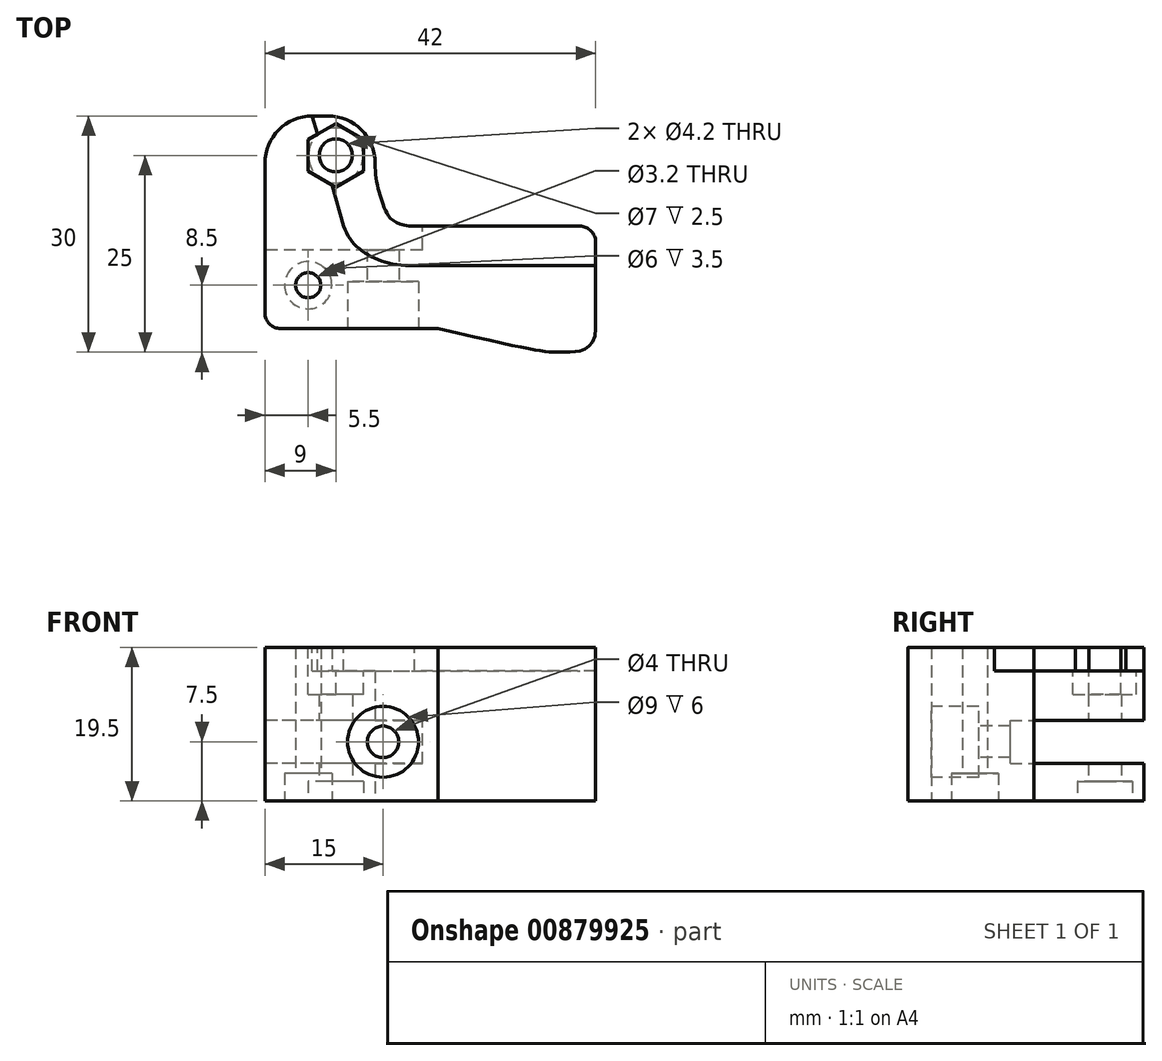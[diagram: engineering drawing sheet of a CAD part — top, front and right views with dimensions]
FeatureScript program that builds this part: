
annotation { "Feature Type Name" : "Feature", "Feature Type Description" : "" }
export const myFeature = defineFeature(function(context is Context, id is Id, definition is map)
    precondition{}
    {
        {
            var Q0;
            Q0=qCreatedBy(makeId("Top.planeOp"),FACE);
            var sketch = newSketch(context, id + "F0", { "sketchPlane" : qUnion([Q0])});
            skLineSegment(sketch, "E0", {"start": v(0, 0) * mm, "end": v(0, 27) * mm});
            skLineSegment(sketch, "E1", {"start": v(0, 27) * mm, "end": v(14, 27) * mm});
            skLineSegment(sketch, "E2", {"start": v(14, 27) * mm, "end": v(14, 13) * mm, "construction": true});
            skLineSegment(sketch, "E3", {"start": v(14, 13) * mm, "end": v(42, 13) * mm, "construction": true});
            skLineSegment(sketch, "E4", {"start": v(42, 13) * mm, "end": v(42, 0) * mm});
            skCircle(sketch, "E5", {"center": v(9, 22) * mm, "radius": 3.5 * mm});
            skCircle(sketch, "E6", {"center": v(5.5, 5.5) * mm, "radius": 3 * mm});
            skLineSegment(sketch, "E7", {"start": v(5.5, 5.5) * mm, "end": v(5.5, 0) * mm, "construction": true});
            skLineSegment(sketch, "E8", {"start": v(0, 0) * mm, "end": v(22, 0) * mm});
            skFitSpline(sketch, "E9", {"points": [v(22, 0) * mm, v(38, -3) * mm, v(42, 0) * mm], "startDerivative": vector(60.61, -13.99) * mm, "endDerivative": vector(0, 25.24) * mm});
            skLineSegment(sketch, "E10", {"start": v(22, 0) * mm, "end": v(35, -3) * mm, "construction": true});
            skCircle(sketch, "E11", {"center": v(5.5, 5.5) * mm, "radius": 1.6 * mm});
            skCircle(sketch, "E12", {"center": v(9, 22) * mm, "radius": 2.1 * mm});
            skFitSpline(sketch, "E13", {"points": [v(14, 21) * mm, v(14.92, 15.97) * mm, v(19, 13) * mm], "startDerivative": vector(0, -11.56) * mm, "endDerivative": vector(17.54, 0) * mm});
            skCircle(sketch, "E14.cCircle", {"center": v(9, 22) * mm, "radius": 3.5 * mm, "construction": true});
            skLineSegment(sketch, "E14.0", {"start": v(9, 26.04) * mm, "end": v(12.5, 24.02) * mm});
            skLineSegment(sketch, "E14.1", {"start": v(12.5, 24.02) * mm, "end": v(12.5, 19.98) * mm});
            skLineSegment(sketch, "E14.2", {"start": v(12.5, 19.98) * mm, "end": v(9, 17.96) * mm});
            skLineSegment(sketch, "E14.3", {"start": v(9, 17.96) * mm, "end": v(5.5, 19.98) * mm});
            skLineSegment(sketch, "E14.4", {"start": v(5.5, 19.98) * mm, "end": v(5.5, 24.02) * mm});
            skLineSegment(sketch, "E14.5", {"start": v(5.5, 24.02) * mm, "end": v(9, 26.04) * mm});
            skPoint(sketch, "E14.0.midPoint", {"position": v(10.75, 25.03) * mm});
            skLineSegment(sketch, "E15", {"start": v(14, 21) * mm, "end": v(14, 27) * mm});
            skLineSegment(sketch, "E16", {"start": v(19, 13) * mm, "end": v(42, 13) * mm});
            skSolve(sketch);
        }
        {
            var Q0;
            Q0=makeQuery(id+"F0.imprint","IMPRINT",FACE,{"disambiguationData":[TD([[makeQuery(id+"F0.imprint","IMPRINT",EDGE,{"derivedFrom":sQuery(id+"F0.wireOp",EDGE,"E6")}),1.0]])]});
            var Q1;
            Q1=makeQuery(id+"F0.imprint","IMPRINT",FACE,{"disambiguationData":[TD([[makeQuery(id+"F0.imprint","IMPRINT",EDGE,{"derivedFrom":sQuery(id+"F0.wireOp",EDGE,"E12")}),-1.0]])]});
            var Q2;
            Q2=makeQuery(id+"F0.imprint","IMPRINT",FACE,{"disambiguationData":[TD([[makeQuery(id+"F0.imprint","IMPRINT",EDGE,{"derivedFrom":sQuery(id+"F0.wireOp",EDGE,"E5")}),1.0]])]});
            var Q3;
            Q3 = qSketchRegion(id + "F2", true);
            var Q4;
            {var subQ0=sQuery(id+"F0.wireOp",EDGE,"E14.0");var subQ1=sQuery(id+"F0.wireOp",EDGE,"E5");var subQ2=makeQuery(id+"F0.imprint","INTERSECT",VERTEX,{"derivedFrom":[subQ1,subQ0]});Q4=makeQuery(id+"F0.imprint","IMPRINT",FACE,{"disambiguationData":[TD([[makeQuery(id+"F0.imprint","IMPRINT",EDGE,{"disambiguationData":[TD([[subQ2,1.0]])],"derivedFrom":subQ1}),-1.0]])]});}
            var Q5;
            {var subQ0=sQuery(id+"F0.wireOp",EDGE,"E14.5");var subQ1=sQuery(id+"F0.wireOp",EDGE,"E5");var subQ2=makeQuery(id+"F0.imprint","INTERSECT",VERTEX,{"derivedFrom":[subQ1,subQ0]});Q5=makeQuery(id+"F0.imprint","IMPRINT",FACE,{"disambiguationData":[TD([[makeQuery(id+"F0.imprint","IMPRINT",EDGE,{"disambiguationData":[TD([[subQ2,1.0]])],"derivedFrom":subQ1}),-1.0]])]});}
            var Q6;
            {var subQ0=sQuery(id+"F0.wireOp",EDGE,"E14.5");var subQ1=sQuery(id+"F0.wireOp",EDGE,"E5");var subQ2=makeQuery(id+"F0.imprint","INTERSECT",VERTEX,{"derivedFrom":[subQ1,subQ0]});Q6=makeQuery(id+"F0.imprint","IMPRINT",FACE,{"disambiguationData":[TD([[makeQuery(id+"F0.imprint","IMPRINT",EDGE,{"disambiguationData":[TD([[subQ2,-1.0]])],"derivedFrom":subQ1}),-1.0]])]});}
            var Q7;
            {var subQ0=sQuery(id+"F0.wireOp",EDGE,"E14.4");var subQ1=sQuery(id+"F0.wireOp",EDGE,"E5");var subQ2=makeQuery(id+"F0.imprint","INTERSECT",VERTEX,{"derivedFrom":[subQ1,subQ0]});Q7=makeQuery(id+"F0.imprint","IMPRINT",FACE,{"disambiguationData":[TD([[makeQuery(id+"F0.imprint","IMPRINT",EDGE,{"disambiguationData":[TD([[subQ2,-1.0]])],"derivedFrom":subQ1}),-1.0]])]});}
            var Q8;
            {var subQ0=sQuery(id+"F0.wireOp",EDGE,"E14.3");var subQ1=sQuery(id+"F0.wireOp",EDGE,"E5");var subQ2=makeQuery(id+"F0.imprint","INTERSECT",VERTEX,{"derivedFrom":[subQ1,subQ0]});Q8=makeQuery(id+"F0.imprint","IMPRINT",FACE,{"disambiguationData":[TD([[makeQuery(id+"F0.imprint","IMPRINT",EDGE,{"disambiguationData":[TD([[subQ2,-1.0]])],"derivedFrom":subQ1}),-1.0]])]});}
            var Q9;
            {var subQ0=sQuery(id+"F0.wireOp",EDGE,"E14.2");var subQ1=sQuery(id+"F0.wireOp",EDGE,"E5");var subQ2=makeQuery(id+"F0.imprint","INTERSECT",VERTEX,{"derivedFrom":[subQ1,subQ0]});Q9=makeQuery(id+"F0.imprint","IMPRINT",FACE,{"disambiguationData":[TD([[makeQuery(id+"F0.imprint","IMPRINT",EDGE,{"disambiguationData":[TD([[subQ2,-1.0]])],"derivedFrom":subQ1}),-1.0]])]});}
            var Q10;
            Q10=makeQuery(id+"F0.imprint","IMPRINT",FACE,{"disambiguationData":[TD([[makeQuery(id+"F0.imprint","IMPRINT",EDGE,{"derivedFrom":sQuery(id+"F0.wireOp",EDGE,"E0")}),-1.0]])]});
            extrude(context, id + "F1", {"entities" : qUnion([Q0, Q1, Q2, Q3, Q4, Q5, Q6, Q7, Q8, Q9, Q10]), "depth" : 19.5 * mm, "offsetDistance" : 25 * mm});
        }
        {
            var Q0;
            Q0=makeQuery(id+"F1.opExtrude","SWEPT_FACE",FACE,{"disambiguationData":[OSD([sQuery(id+"F0.wireOp",EDGE,"E0")])]});
            var sketch = newSketch(context, id + "F2", { "sketchPlane" : qUnion([Q0])});
            skLineSegment(sketch, "E17.bottom", {"start": v(-10, 4.75) * mm, "end": v(-27, 4.75) * mm});
            skLineSegment(sketch, "E17.top", {"start": v(-10, 10.25) * mm, "end": v(-27, 10.25) * mm});
            skLineSegment(sketch, "E17.left", {"start": v(-10, 4.75) * mm, "end": v(-10, 10.25) * mm});
            skLineSegment(sketch, "E17.right", {"start": v(-27, 4.75) * mm, "end": v(-27, 10.25) * mm});
            skPoint(sketch, "E17.middle", {"position": v(-18.5, 7.5) * mm});
            skPoint(sketch, "E18", {"position": v(-25.5, 7.5) * mm});
            skSolve(sketch);
        }
        {
            var Q0;
            Q0=makeQuery(id+"F1.opExtrude","CAP_FACE",FACE,{"disambiguationData":[OSD([sQuery(id+"F0.wireOp",EDGE,"E0"),sQuery(id+"F0.wireOp",EDGE,"E1"),sQuery(id+"F0.wireOp",EDGE,"E4"),sQuery(id+"F0.wireOp",EDGE,"E6"),sQuery(id+"F0.wireOp",EDGE,"E8"),sQuery(id+"F0.wireOp",EDGE,"E9"),sQuery(id+"F0.wireOp",EDGE,"E12"),sQuery(id+"F0.wireOp",EDGE,"E13"),sQuery(id+"F0.wireOp",EDGE,"E15"),sQuery(id+"F0.wireOp",EDGE,"E16")])],"isStart":false});
            var sketch = newSketch(context, id + "F3", { "sketchPlane" : qUnion([Q0])});
            skCircle(sketch, "E19.0", {"center": v(9, 22) * mm, "radius": 3.5 * mm});
            skLineSegment(sketch, "E20.0", {"start": v(9, 26.04) * mm, "end": v(12.5, 24.02) * mm});
            skLineSegment(sketch, "E21.0", {"start": v(5.5, 24.02) * mm, "end": v(9, 26.04) * mm});
            skLineSegment(sketch, "E22.0", {"start": v(5.5, 19.98) * mm, "end": v(5.5, 24.02) * mm});
            skLineSegment(sketch, "E23.0", {"start": v(9, 17.96) * mm, "end": v(5.5, 19.98) * mm});
            skLineSegment(sketch, "E24.0", {"start": v(12.5, 19.98) * mm, "end": v(9, 17.96) * mm});
            skLineSegment(sketch, "E25.0", {"start": v(12.5, 24.02) * mm, "end": v(12.5, 19.98) * mm});
            skSolve(sketch);
        }
        {
            var Q0;
            Q0=makeQuery(id+"F0.imprint","IMPRINT",FACE,{"disambiguationData":[TD([[makeQuery(id+"F0.imprint","IMPRINT",EDGE,{"derivedFrom":sQuery(id+"F0.wireOp",EDGE,"E0")}),-1.0]])]});
            var sketch = newSketch(context, id + "F4", { "sketchPlane" : qUnion([Q0])});
            skSolve(sketch);
        }
        {
            var Q0;
            Q0 = qSketchRegion(id + "F4", true);
            var Q1;
            Q1=makeQuery(id+"F0.imprint","IMPRINT",FACE,{"disambiguationData":[TD([[makeQuery(id+"F0.imprint","IMPRINT",EDGE,{"derivedFrom":sQuery(id+"F0.wireOp",EDGE,"E5")}),1.0]])]});
            var Q2;
            Q2=makeQuery(id+"F4.imprint","IMPRINT",FACE,{"disambiguationData":[TD([[makeQuery(id+"F4.imprint","IMPRINT",EDGE,{"derivedFrom":makeQuery(id+"F0.imprint","IMPRINT",EDGE,{"derivedFrom":sQuery(id+"F0.wireOp",EDGE,"E5")})}),1.0]])]});
            var Q3;
            Q3=makeQuery(id+"F0.imprint","IMPRINT",FACE,{"disambiguationData":[TD([[makeQuery(id+"F0.imprint","IMPRINT",EDGE,{"derivedFrom":sQuery(id+"F0.wireOp",EDGE,"E12")}),-1.0]])]});
            extrude(context, id + "F5", {"entities" : qUnion([Q0, Q1, Q2, Q3]), "operationType" : NewBodyOperationType.REMOVE, "depth" : 2.5 * mm, "offsetDistance" : 25 * mm});
        }
        {
            var Q0;
            Q0 = qSketchRegion(id + "F4", true);
            var Q1;
            Q1=makeQuery(id+"F0.imprint","IMPRINT",FACE,{"disambiguationData":[TD([[makeQuery(id+"F0.imprint","IMPRINT",EDGE,{"derivedFrom":sQuery(id+"F0.wireOp",EDGE,"E6")}),1.0]])]});
            extrude(context, id + "F6", {"entities" : qUnion([Q0, Q1]), "operationType" : NewBodyOperationType.REMOVE, "depth" : 3.5 * mm, "offsetDistance" : 25 * mm});
        }
        {
            var Q0;
            Q0=makeQuery(id+"F1.opExtrude","SWEPT_FACE",FACE,{"disambiguationData":[OSD([sQuery(id+"F0.wireOp",EDGE,"E8")])]});
            var sketch = newSketch(context, id + "F7", { "sketchPlane" : qUnion([Q0])});
            skCircle(sketch, "E26", {"center": v(15, 7.5) * mm, "radius": 4.5 * mm});
            skCircle(sketch, "E27", {"center": v(15, 7.5) * mm, "radius": 2 * mm});
            skSolve(sketch);
        }
        {
            var Q0;
            Q0=makeQuery(id+"F7.imprint","IMPRINT",FACE,{"disambiguationData":[TD([[makeQuery(id+"F7.imprint","IMPRINT",EDGE,{"derivedFrom":sQuery(id+"F7.wireOp",EDGE,"E27")}),1.0]])]});
            var Q1;
            Q1=sQuery(id+"F7.wireOp",EDGE,"E27");
            extrude(context, id + "F8", {"entities" : qUnion([Q0]), "operationType" : NewBodyOperationType.REMOVE, "surfaceEntities" : qUnion([Q1]), "endBound" : BoundingType.THROUGH_ALL, "oppositeDirection" : true, "depth" : 25 * mm, "offsetDistance" : 25 * mm});
        }
        {
            var Q0;
            Q0=makeQuery(id+"F7.imprint","IMPRINT",FACE,{"disambiguationData":[TD([[makeQuery(id+"F7.imprint","IMPRINT",EDGE,{"derivedFrom":sQuery(id+"F7.wireOp",EDGE,"E26")}),1.0]])]});
            var Q1;
            Q1=sQuery(id+"F7.wireOp",EDGE,"E26");
            extrude(context, id + "F9", {"entities" : qUnion([Q0]), "operationType" : NewBodyOperationType.REMOVE, "surfaceEntities" : qUnion([Q1]), "oppositeDirection" : true, "depth" : 6 * mm, "offsetDistance" : 25 * mm});
        }
        {
            var Q0;
            {var subQ0=sQuery(id+"F0.wireOp",EDGE,"E0");var subQ1=sQuery(id+"F0.wireOp",EDGE,"E1");Q0=makeQuery(id+"Fyu53mA3qCWFFU0_1.boolean.opBoolean","SPLIT",EDGE,{"disambiguationData":[TD([makeQuery(id+"Fyu53mA3qCWFFU0_1.opExtrude","SWEPT_FACE",FACE,{"disambiguationData":[OSD([sQuery(id+"F2.wireOp",EDGE,"E17.top")])]})])],"derivedFrom":makeQuery(id+"F1.opExtrude","SWEPT_EDGE",EDGE,{"disambiguationData":[OSD([subQ0,subQ1])]})});}
            fillet(context, id + "F10", {"entities" : qUnion([Q0]), "radius" : 6 * mm, "tangentPropagation" : true, "allowEdgeOverflow" : false});
        }
        {
            var Q0;
            Q0=makeQuery(id+"F1.opExtrude","CAP_FACE",FACE,{"disambiguationData":[OSD([sQuery(id+"F0.wireOp",EDGE,"E0"),sQuery(id+"F0.wireOp",EDGE,"E1"),sQuery(id+"F0.wireOp",EDGE,"E4"),sQuery(id+"F0.wireOp",EDGE,"E8"),sQuery(id+"F0.wireOp",EDGE,"E9"),sQuery(id+"F0.wireOp",EDGE,"E11"),sQuery(id+"F0.wireOp",EDGE,"E12"),sQuery(id+"F0.wireOp",EDGE,"E13"),sQuery(id+"F0.wireOp",EDGE,"E15"),sQuery(id+"F0.wireOp",EDGE,"E16")])],"isStart":false});
            var sketch = newSketch(context, id + "F11", { "sketchPlane" : qUnion([Q0])});
            skLineSegment(sketch, "E28", {"start": v(42, 8) * mm, "end": v(19, 8) * mm});
            skLineSegment(sketch, "E29", {"start": v(19, 13) * mm, "end": v(19, 8) * mm, "construction": true});
            skLineSegment(sketch, "E30", {"start": v(6, 27) * mm, "end": v(9.99, 13) * mm});
            skFitSpline(sketch, "E31", {"points": [v(9.99, 13) * mm, v(12.95, 9.46) * mm, v(19, 8) * mm], "startDerivative": vector(3.35, -10.08) * mm, "endDerivative": vector(13.74, 0.35) * mm});
            skSolve(sketch);
        }
        {
            var Q0;
            {var subQ5=sQuery(id+"F11.wireOp",EDGE,"E28");Q0=makeQuery(id+"F11.imprint","IMPRINT",FACE,{"disambiguationData":[TD([[makeQuery(id+"F11.imprint","IMPRINT",EDGE,{"derivedFrom":subQ5}),-1.0]])]});}
            extrude(context, id + "F12", {"entities" : qUnion([Q0]), "operationType" : NewBodyOperationType.REMOVE, "oppositeDirection" : true, "depth" : 3 * mm, "offsetDistance" : 25 * mm});
        }
        {
            var Q0;
            {var subQ0=sQuery(id+"F0.wireOp",EDGE,"E15");var subQ1=sQuery(id+"F0.wireOp",EDGE,"E1");Q0=makeQuery(id+"Fyu53mA3qCWFFU0_1.boolean.opBoolean","SPLIT",EDGE,{"disambiguationData":[TD([makeQuery(id+"Fyu53mA3qCWFFU0_1.opExtrude","SWEPT_FACE",FACE,{"disambiguationData":[OSD([sQuery(id+"F2.wireOp",EDGE,"E17.bottom")])]})])],"derivedFrom":makeQuery(id+"F1.opExtrude","SWEPT_EDGE",EDGE,{"disambiguationData":[OSD([subQ1,subQ0])]})});}
            fillet(context, id + "F13", {"entities" : qUnion([Q0]), "radius" : 6 * mm, "tangentPropagation" : true, "allowEdgeOverflow" : false});
        }
        {
            var Q0;
            Q0=makeQuery(id+"F1.opExtrude","SWEPT_EDGE",EDGE,{"disambiguationData":[OSD([sQuery(id+"F0.wireOp",EDGE,"E4"),sQuery(id+"F0.wireOp",EDGE,"E16")])]});
            fillet(context, id + "F14", {"entities" : qUnion([Q0]), "radius" : 2 * mm, "tangentPropagation" : true, "allowEdgeOverflow" : false});
        }
        {
            var Q0;
            Q0=makeQuery(id+"F1.opExtrude","SWEPT_EDGE",EDGE,{"disambiguationData":[OSD([sQuery(id+"F0.wireOp",EDGE,"E0"),sQuery(id+"F0.wireOp",EDGE,"E8")])]});
            fillet(context, id + "F15", {"entities" : qUnion([Q0]), "radius" : 2 * mm, "tangentPropagation" : true, "allowEdgeOverflow" : false});
        }
        {
            var Q0;
            Q0=makeQuery(id+"F2.imprint","IMPRINT",FACE,{"disambiguationData":[TD([[makeQuery(id+"F2.imprint","IMPRINT",EDGE,{"derivedFrom":sQuery(id+"F2.wireOp",EDGE,"E17.bottom")}),-1.0]])]});
            extrude(context, id + "F16", {"entities" : qUnion([Q0]), "operationType" : NewBodyOperationType.REMOVE, "oppositeDirection" : true, "depth" : 20 * mm, "offsetDistance" : 25 * mm});
        }
        {
            var Q0;
            {var subQ0=sQuery(id+"F3.wireOp",EDGE,"E20.0");var subQ1=sQuery(id+"F3.wireOp",EDGE,"E19.0");var subQ2=makeQuery(id+"F3.imprint","INTERSECT",VERTEX,{"derivedFrom":[subQ1,subQ0]});Q0=makeQuery(id+"F3.imprint","IMPRINT",FACE,{"disambiguationData":[TD([[makeQuery(id+"F3.imprint","IMPRINT",EDGE,{"disambiguationData":[TD([[subQ2,-1.0]])],"derivedFrom":subQ1}),-1.0]])]});}
            var Q1;
            {var subQ0=sQuery(id+"F3.wireOp",EDGE,"E20.0");var subQ1=sQuery(id+"F3.wireOp",EDGE,"E19.0");var subQ2=makeQuery(id+"F3.imprint","INTERSECT",VERTEX,{"derivedFrom":[subQ1,subQ0]});Q1=makeQuery(id+"F3.imprint","IMPRINT",FACE,{"disambiguationData":[TD([[makeQuery(id+"F3.imprint","IMPRINT",EDGE,{"disambiguationData":[TD([[subQ2,1.0]])],"derivedFrom":subQ1}),-1.0]])]});}
            var Q2;
            Q2=makeQuery(id+"F3.imprint","IMPRINT",FACE,{"disambiguationData":[TD([[makeQuery(id+"F3.imprint","IMPRINT",EDGE,{"derivedFrom":makeQuery(id+"F1.opExtrude","CAP_EDGE",EDGE,{"disambiguationData":[OSD([sQuery(id+"F0.wireOp",EDGE,"E12")])],"isStart":false})}),-1.0]])]});
            var Q3;
            {var subQ0=sQuery(id+"F3.wireOp",EDGE,"E21.0");var subQ1=sQuery(id+"F3.wireOp",EDGE,"E19.0");var subQ2=makeQuery(id+"F3.imprint","INTERSECT",VERTEX,{"derivedFrom":[subQ1,subQ0]});Q3=makeQuery(id+"F3.imprint","IMPRINT",FACE,{"disambiguationData":[TD([[makeQuery(id+"F3.imprint","IMPRINT",EDGE,{"disambiguationData":[TD([[subQ2,-1.0]])],"derivedFrom":subQ1}),-1.0]])]});}
            var Q4;
            {var subQ0=sQuery(id+"F3.wireOp",EDGE,"E22.0");var subQ1=sQuery(id+"F3.wireOp",EDGE,"E19.0");var subQ2=makeQuery(id+"F3.imprint","INTERSECT",VERTEX,{"derivedFrom":[subQ1,subQ0]});Q4=makeQuery(id+"F3.imprint","IMPRINT",FACE,{"disambiguationData":[TD([[makeQuery(id+"F3.imprint","IMPRINT",EDGE,{"disambiguationData":[TD([[subQ2,-1.0]])],"derivedFrom":subQ1}),-1.0]])]});}
            var Q5;
            {var subQ0=sQuery(id+"F3.wireOp",EDGE,"E23.0");var subQ1=sQuery(id+"F3.wireOp",EDGE,"E19.0");var subQ2=makeQuery(id+"F3.imprint","INTERSECT",VERTEX,{"derivedFrom":[subQ1,subQ0]});Q5=makeQuery(id+"F3.imprint","IMPRINT",FACE,{"disambiguationData":[TD([[makeQuery(id+"F3.imprint","IMPRINT",EDGE,{"disambiguationData":[TD([[subQ2,-1.0]])],"derivedFrom":subQ1}),-1.0]])]});}
            var Q6;
            {var subQ0=sQuery(id+"F3.wireOp",EDGE,"E25.0");var subQ1=sQuery(id+"F3.wireOp",EDGE,"E19.0");var subQ2=makeQuery(id+"F3.imprint","INTERSECT",VERTEX,{"derivedFrom":[subQ1,subQ0]});Q6=makeQuery(id+"F3.imprint","IMPRINT",FACE,{"disambiguationData":[TD([[makeQuery(id+"F3.imprint","IMPRINT",EDGE,{"disambiguationData":[TD([[subQ2,1.0]])],"derivedFrom":subQ1}),-1.0]])]});}
            var Q7;
            Q7=sQuery(id+"F3.wireOp",EDGE,"E23.0");
            var Q8;
            Q8=sQuery(id+"F3.wireOp",EDGE,"E24.0");
            var Q9;
            Q9=sQuery(id+"F3.wireOp",EDGE,"E25.0");
            var Q10;
            Q10=sQuery(id+"F3.wireOp",EDGE,"E20.0");
            var Q11;
            Q11=sQuery(id+"F3.wireOp",EDGE,"E21.0");
            var Q12;
            Q12=sQuery(id+"F3.wireOp",EDGE,"E22.0");
            extrude(context, id + "F17", {"entities" : qUnion([Q0, Q1, Q2, Q3, Q4, Q5, Q6]), "operationType" : NewBodyOperationType.REMOVE, "surfaceEntities" : qUnion([Q7, Q8, Q9, Q10, Q11, Q12]), "oppositeDirection" : true, "depth" : 6 * mm, "offsetDistance" : 25 * mm});
        }
    });
